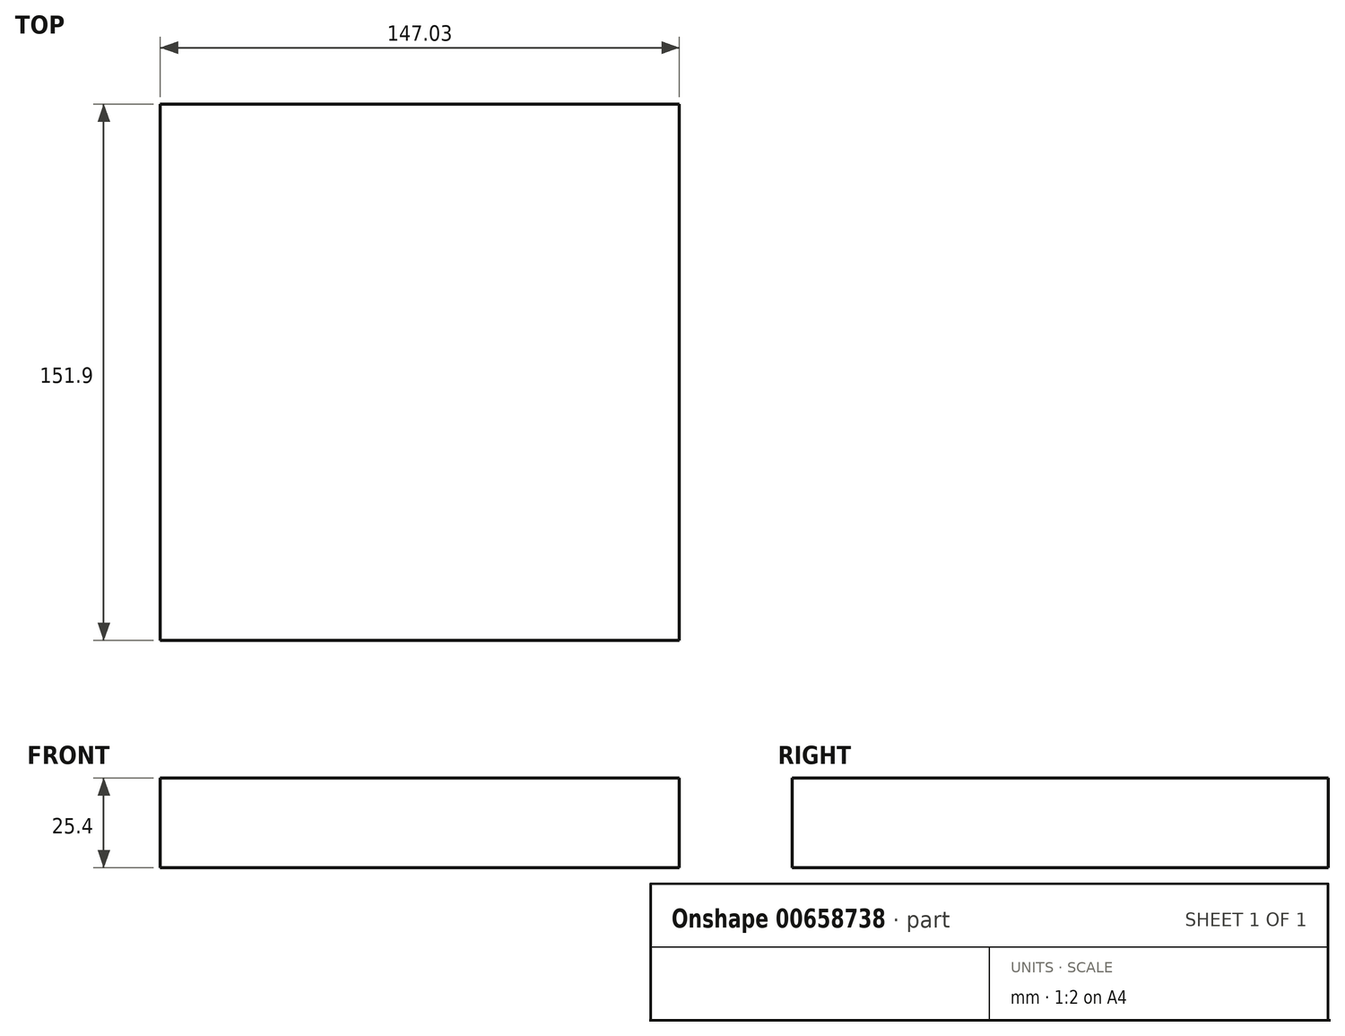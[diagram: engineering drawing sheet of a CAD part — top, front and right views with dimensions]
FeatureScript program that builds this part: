
annotation { "Feature Type Name" : "Feature", "Feature Type Description" : "" }
export const myFeature = defineFeature(function(context is Context, id is Id, definition is map)
    precondition{}
    {
        {
            var Q0;
            Q0=qCreatedBy(makeId("Top.planeOp"),FACE);
            var sketch = newSketch(context, id + "F0", { "sketchPlane" : qUnion([Q0])});
            skLineSegment(sketch, "E0.bottom", {"start": v(-74.14, 72.08) * mm, "end": v(72.89, 72.08) * mm});
            skLineSegment(sketch, "E0.top", {"start": v(-74.14, -79.82) * mm, "end": v(72.89, -79.82) * mm});
            skLineSegment(sketch, "E0.left", {"start": v(-74.14, 72.08) * mm, "end": v(-74.14, -79.82) * mm});
            skLineSegment(sketch, "E0.right", {"start": v(72.89, 72.08) * mm, "end": v(72.89, -79.82) * mm});
            skSolve(sketch);
        }
        {
            var Q0;
            Q0 = qSketchRegion(id + "F0", true);
            extrude(context, id + "F1", {"entities" : qUnion([Q0]), "depth" : 25.4 * mm, "offsetDistance" : 25.4 * mm});
        }
    });
